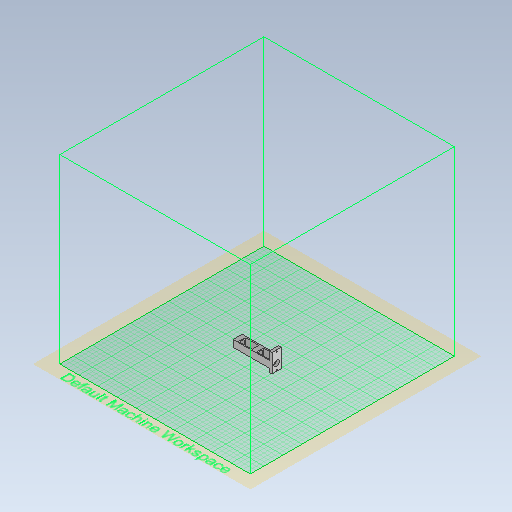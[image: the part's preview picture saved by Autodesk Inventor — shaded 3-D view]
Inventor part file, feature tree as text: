
AUTODESK INVENTOR PART (.ipt)
format: ipt  version: 2020.3 (Build 243373000, 373)  size: 331,264 bytes
history: native  units: mm
features: sketch x4, extrude x4, plane x1
ambient origin geometry x8: Origin, YZ Plane, XZ Plane, XY Plane, X Axis, Y Axis, Z Axis, Center Point
bodies: Body1 (feature_tree)
feature tree (9):
  sketch  "Sketch1"  dims[d10=41.0mm d11=22.0mm]
  extrude  "Extrusion5"  Depth=22.0mm
  extrude  "Extrusion6"  Depth=10.0mm
  extrude  "Extrusion7"  Depth=8.0mm
  plane  "Work Plane1"
  sketch  "Sketch5"  dims[d17=8.0mm d18=2.8mm]
  extrude  "Extrusion8"  Depth=10.0mm
  sketch  "Sketch4"  dims[d12=15.0mm d15=10.0mm]
  sketch  "Sketch6"  dims[d19=2.8mm d20=12.4mm d22=10.0mm d23=10.0mm d24=35.0mm d25=3.0mm d26=7.5mm d27=17.0mm d28=3.0mm d29=6.0mm d30=0.0mm d31=50.0mm d32=0.0mm d33=10.0mm d34=0.0mm d35=25.0mm d36=10.0mm d37=0.0mm d38=12.4mm d39=12.4mm]
